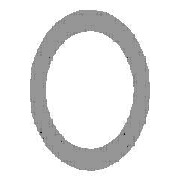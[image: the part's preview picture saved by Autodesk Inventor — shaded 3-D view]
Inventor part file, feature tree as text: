
AUTODESK INVENTOR PART (.ipt)
format: ipt  version: 2013 (Build 170138000, 138)  size: 109,568 bytes
history: native  units: mm (DEFAULTED — no unit token found)
features: other x4, sketch x3, plane x1
ambient origin geometry x8: Origin, YZ Plane, XZ Plane, XY Plane, X Axis, Y Axis, Z Axis, Center Point
bodies: Solid1 (feature_tree), Body (feature_tree)
feature tree (8):
  parser-record x1  (decoder bookkeeping rows leaked as tree rows — omitted from the tree; the rows remain in map.json)
  other  "Driven Length"
  other  "Start plane"
  other  "End plane"
  sketch  "Sketch"  dims[d2=508.0mm d3=0.0mm d4=-0.0mm d5=508.0mm d6=90.0deg d7=508.0mm]
  sketch  "Sketch3"  dims[d0=42.164mm]
  plane  "Work Plane3"
  sketch  "Sketch4"  dims[d1=3.556mm]
